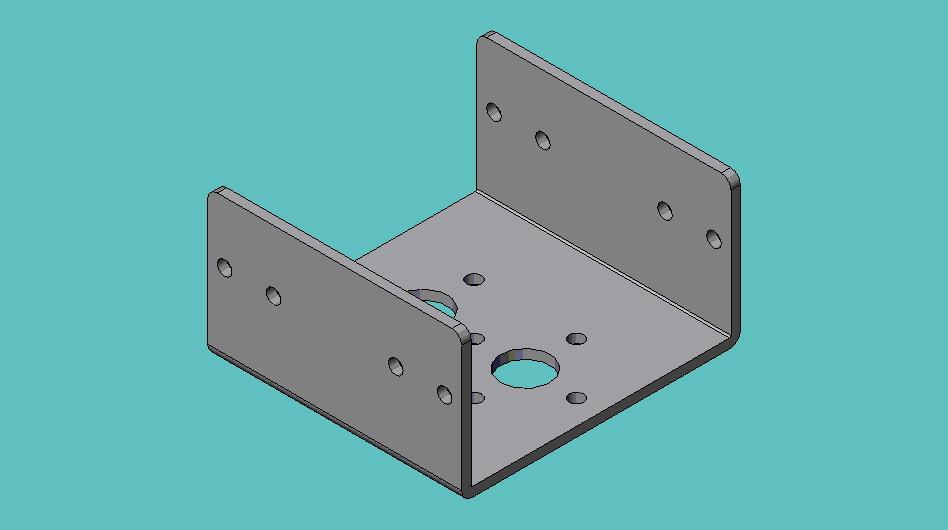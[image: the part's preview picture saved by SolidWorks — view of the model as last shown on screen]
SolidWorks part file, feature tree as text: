
SOLIDWORKS PART (.sldprt)
format: sldprt  version: not decoded by parser v0  size: 251,904 bytes
history: native  units: mm
features: sketch x3, cut_extrude x2, material x1, extrude x1, fillet x1 (+12 scaffold rows collapsed)
feature tree (20):
  scaffold x12  (default folders/planes/origin — collapsed)
  material  "Material <not specified>"
  sketch  "Sketch1"  dims[c1.D1=3.1115mm c1.D2=1.5875mm c2.D1=1.778mm c2.D2=0.254mm c3.D1=22.6187mm c4.D1=90.0deg c5.D1=1.524mm]
  extrude  "Extrude1"  Depth=20.6375mm
  sketch  "Sketch2"  dims[D1=9.7028mm]
  cut_extrude  "Cut-Extrude1"  Depth=20.6375mm
  sketch  "Sketch3"  dims[D1=10.7188mm]
  cut_extrude  "Cut-Extrude2"  [1 undecoded]
  fillet  "Fillet1"  Radius=1.5875mm
decode coverage: 6 of 7 modeling features carry decoded parameters
note: 1 parameter value undecoded
note: suppression state not decoded; provenance and decode notes live in map.json
